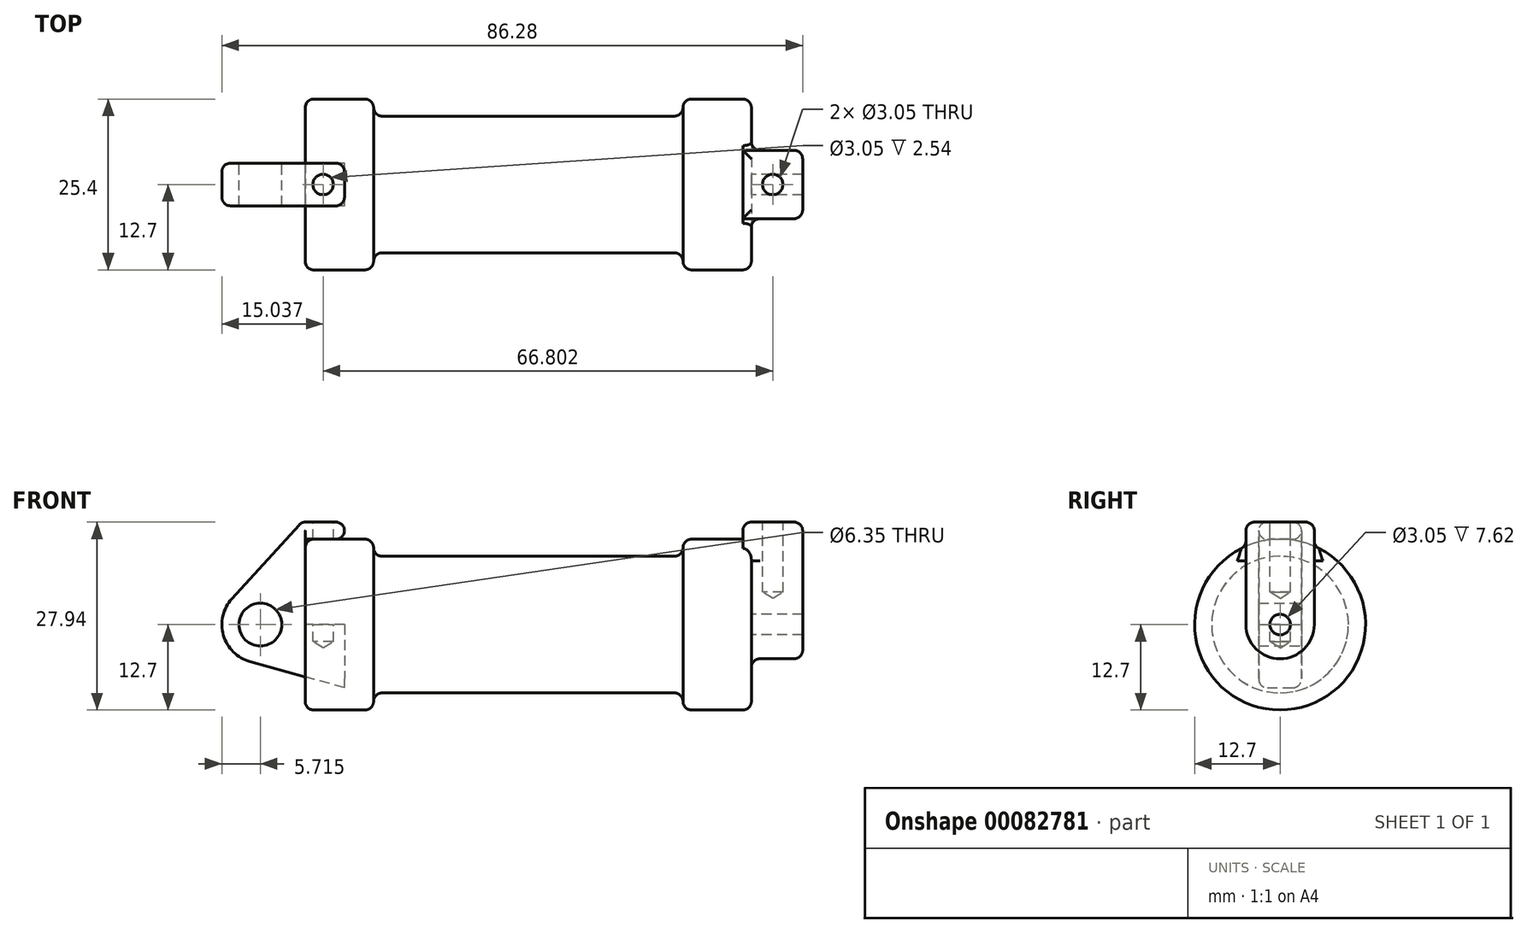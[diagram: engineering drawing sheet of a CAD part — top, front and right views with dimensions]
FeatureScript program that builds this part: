
annotation { "Feature Type Name" : "Feature", "Feature Type Description" : "" }
export const myFeature = defineFeature(function(context is Context, id is Id, definition is map)
    precondition{}
    {
        {
            var Q0;
            Q0=qCreatedBy(makeId("Front.planeOp"),FACE);
            var sketch = newSketch(context, id + "F0", { "sketchPlane" : qUnion([Q0])});
            skLineSegment(sketch, "E0", {"start": v(0, 0) * mm, "end": v(0, 12.7) * mm});
            skLineSegment(sketch, "E1", {"start": v(0, 12.7) * mm, "end": v(10.16, 12.7) * mm});
            skLineSegment(sketch, "E2", {"start": v(10.16, 12.7) * mm, "end": v(10.16, 10.16) * mm});
            skLineSegment(sketch, "E3", {"start": v(10.16, 10.16) * mm, "end": v(56.13, 10.16) * mm});
            skLineSegment(sketch, "E4", {"start": v(56.13, 10.16) * mm, "end": v(56.13, 12.7) * mm});
            skLineSegment(sketch, "E5", {"start": v(56.13, 12.7) * mm, "end": v(66.3, 12.7) * mm});
            skLineSegment(sketch, "E6", {"start": v(66.3, 12.7) * mm, "end": v(66.3, 0) * mm});
            skLineSegment(sketch, "E7", {"start": v(66.3, 0) * mm, "end": v(0, 0) * mm});
            skLineSegment(sketch, "E8", {"start": v(5.84, 15.24) * mm, "end": v(-0.5, 15.24) * mm});
            skLineSegment(sketch, "E9", {"start": v(-0.5, 15.24) * mm, "end": v(-10.88, 3.85) * mm});
            skLineSegment(sketch, "E10", {"start": v(0, 0) * mm, "end": v(-6.65, 0) * mm});
            skCircle(sketch, "E11", {"center": v(-6.65, 0) * mm, "radius": 5.72 * mm});
            skCircle(sketch, "E12", {"center": v(-6.65, 0) * mm, "radius": 3.18 * mm});
            skLineSegment(sketch, "E13", {"start": v(5.84, 15.24) * mm, "end": v(5.84, -9.4) * mm});
            skLineSegment(sketch, "E14", {"start": v(5.84, -9.4) * mm, "end": v(-8.18, -5.5) * mm});
            skSolve(sketch);
        }
        {
            var Q0;
            {var subQ0=sQuery(id+"F0.wireOp",EDGE,"E0");Q0=makeQuery(id+"F0.imprint","IMPRINT",FACE,{"disambiguationData":[TD([[makeQuery(id+"F0.imprint","IMPRINT",EDGE,{"derivedFrom":subQ0}),-1.0]])]});}
            var Q1;
            {var subQ0=sQuery(id+"F0.wireOp",EDGE,"E2");Q1=makeQuery(id+"F0.imprint","IMPRINT",FACE,{"disambiguationData":[TD([[makeQuery(id+"F0.imprint","IMPRINT",EDGE,{"derivedFrom":subQ0}),-1.0]])]});}
            var Q2;
            Q2=sQuery(id+"F0.wireOp",EDGE,"E7");
            revolve(context, id + "F1", {"entities" : qUnion([Q0, Q1]), "axis" : qUnion([Q2]), "revolveType" : RevolveType.FULL});
        }
        {
            var Q0;
            {var subQ3=sQuery(id+"F0.wireOp",EDGE,"E0");Q0=makeQuery(id+"F0.imprint","IMPRINT",FACE,{"disambiguationData":[TD([[makeQuery(id+"F0.imprint","IMPRINT",EDGE,{"derivedFrom":subQ3}),1.0]])]});}
            var Q1;
            {var subQ4=sQuery(id+"F0.wireOp",EDGE,"E12");Q1=makeQuery(id+"F0.imprint","IMPRINT",FACE,{"disambiguationData":[TD([[makeQuery(id+"F0.imprint","IMPRINT",EDGE,{"derivedFrom":subQ4}),-1.0]])]});}
            var Q2;
            {var subQ0=sQuery(id+"F0.wireOp",EDGE,"E14");Q2=makeQuery(id+"F0.imprint","IMPRINT",FACE,{"disambiguationData":[TD([[makeQuery(id+"F0.imprint","IMPRINT",EDGE,{"derivedFrom":subQ0}),-1.0]])]});}
            extrude(context, id + "F2", {"entities" : qUnion([Q0, Q1, Q2]), "endBound" : BoundingType.SYMMETRIC, "depth" : 6.35 * mm});
        }
        {
            var Q0;
            Q0=makeQuery(id+"F1.opRevolve","SWEPT_FACE",FACE,{"disambiguationData":[OSD([sQuery(id+"F0.wireOp",EDGE,"E6")])]});
            var sketch = newSketch(context, id + "F3", { "sketchPlane" : qUnion([Q0])});
            skCircle(sketch, "E15", {"center": v(0, 0) * mm, "radius": 5.08 * mm});
            skCircle(sketch, "E16", {"center": v(0, 0) * mm, "radius": 1.52 * mm});
            skLineSegment(sketch, "E17", {"start": v(-5.08, 0) * mm, "end": v(-5.08, 15.24) * mm});
            skLineSegment(sketch, "E18", {"start": v(5.08, 0) * mm, "end": v(5.08, 15.24) * mm});
            skLineSegment(sketch, "E19", {"start": v(5.08, 15.24) * mm, "end": v(-5.08, 15.24) * mm});
            skSolve(sketch);
        }
        {
            var Q0;
            {var subQ0=sQuery(id+"F3.wireOp",EDGE,"E19");Q0=makeQuery(id+"F3.imprint","IMPRINT",FACE,{"disambiguationData":[TD([[makeQuery(id+"F3.imprint","IMPRINT",EDGE,{"derivedFrom":subQ0}),1.0]])]});}
            var Q1;
            {var subQ0=sQuery(id+"F3.wireOp",EDGE,"E17");var subQ1=sQuery(id+"F3.wireOp",EDGE,"E15");var subQ2=makeQuery(id+"F3.imprint","INTERSECT",VERTEX,{"derivedFrom":[subQ1,subQ0]});Q1=makeQuery(id+"F3.imprint","IMPRINT",FACE,{"disambiguationData":[TD([[makeQuery(id+"F3.imprint","IMPRINT",EDGE,{"disambiguationData":[TD([[subQ2,1.0]])],"derivedFrom":subQ1}),-1.0]])]});}
            var Q2;
            Q2=makeQuery(id+"F3.imprint","IMPRINT",FACE,{"disambiguationData":[TD([[makeQuery(id+"F3.imprint","IMPRINT",EDGE,{"derivedFrom":sQuery(id+"F3.wireOp",EDGE,"E16")}),-1.0]])]});
            extrude(context, id + "F4", {"entities" : qUnion([Q0, Q1, Q2]), "operationType" : NewBodyOperationType.ADD, "depth" : 7.62 * mm, "hasSecondDirection" : true, "secondDirectionOppositeDirection" : true, "secondDirectionDepth" : 1.27 * mm});
        }
        {
            var Q0;
            Q0=makeQuery(id+"F4.opExtrude","SWEPT_FACE",FACE,{"disambiguationData":[OSD([sQuery(id+"F3.wireOp",EDGE,"E19")])]});
            var sketch = newSketch(context, id + "F5", { "sketchPlane" : qUnion([Q0])});
            skCircle(sketch, "E20", {"center": v(2.67, 0) * mm, "radius": 1.52 * mm});
            skPoint(sketch, "E20.centerSnap0", {"position": v(2.67, 3.18) * mm});
            skPoint(sketch, "E21.centerSnap0", {"position": v(69.47, 5.08) * mm});
            skSolve(sketch);
        }
        {
            var Q0;
            Q0=sQuery(id+"F5.wireOp",VERTEX,"E20.center");
            var Q1;
            Q1=makeQuery(id+"F2.opExtrude","SWEPT_BODY",BODY,{"disambiguationData":[OSD([sQuery(id+"F0.wireOp",EDGE,"E0"),sQuery(id+"F0.wireOp",EDGE,"E1"),sQuery(id+"F0.wireOp",EDGE,"E7"),sQuery(id+"F0.wireOp",EDGE,"E8"),sQuery(id+"F0.wireOp",EDGE,"E9"),sQuery(id+"F0.wireOp",EDGE,"E11"),sQuery(id+"F0.wireOp",EDGE,"E12"),sQuery(id+"F0.wireOp",EDGE,"E13"),sQuery(id+"F0.wireOp",EDGE,"E14")])]});
            hole(context, id + "F6", {"style" : HoleStyle.SIMPLE, "endStyle" : HoleEndStyle.BLIND, "holeDiameter" : 3.05 * mm, "holeDepth" : 17.78 * mm, "locations" : qUnion([Q0]), "scope" : qUnion([Q1])});
        }
        {
            var Q0;
            Q0=makeQuery(id+"F4.opExtrude","SWEPT_FACE",FACE,{"disambiguationData":[OSD([sQuery(id+"F3.wireOp",EDGE,"E19")])]});
            var sketch = newSketch(context, id + "F7", { "sketchPlane" : qUnion([Q0])});
            skCircle(sketch, "E22", {"center": v(69.47, 0) * mm, "radius": 1.52 * mm});
            skPoint(sketch, "E22.centerSnap0", {"position": v(69.47, 5.08) * mm});
            skPoint(sketch, "E22.centerSnap1", {"position": v(65.02, 0) * mm});
            skSolve(sketch);
        }
        {
            var Q0;
            Q0=sQuery(id+"F7.wireOp",VERTEX,"E22.center");
            var Q1;
            Q1=makeQuery(id+"F1.opRevolve","SWEPT_BODY",BODY,{"disambiguationData":[OSD([sQuery(id+"F0.wireOp",EDGE,"E0"),sQuery(id+"F0.wireOp",EDGE,"E1"),sQuery(id+"F0.wireOp",EDGE,"E2"),sQuery(id+"F0.wireOp",EDGE,"E3"),sQuery(id+"F0.wireOp",EDGE,"E4"),sQuery(id+"F0.wireOp",EDGE,"E5"),sQuery(id+"F0.wireOp",EDGE,"E6"),sQuery(id+"F0.wireOp",EDGE,"E7")])]});
            hole(context, id + "F8", {"style" : HoleStyle.SIMPLE, "endStyle" : HoleEndStyle.BLIND, "holeDiameter" : 3.05 * mm, "holeDepth" : 10.4 * mm, "locations" : qUnion([Q0]), "scope" : qUnion([Q1])});
        }
        {
            var Q0;
            Q0=makeQuery(id+"F1.opRevolve","SWEPT_EDGE",EDGE,{"disambiguationData":[OSD([sQuery(id+"F0.wireOp",EDGE,"E2"),sQuery(id+"F0.wireOp",EDGE,"E3")])]});
            var Q1;
            Q1=makeQuery(id+"F1.opRevolve","SWEPT_EDGE",EDGE,{"disambiguationData":[OSD([sQuery(id+"F0.wireOp",EDGE,"E1"),sQuery(id+"F0.wireOp",EDGE,"E2")])]});
            var Q2;
            Q2=makeQuery(id+"F1.opRevolve","SWEPT_EDGE",EDGE,{"disambiguationData":[OSD([sQuery(id+"F0.wireOp",EDGE,"E0"),sQuery(id+"F0.wireOp",EDGE,"E1")])]});
            var Q3;
            Q3=makeQuery(id+"F1.opRevolve","SWEPT_EDGE",EDGE,{"disambiguationData":[OSD([sQuery(id+"F0.wireOp",EDGE,"E4"),sQuery(id+"F0.wireOp",EDGE,"E5")])]});
            var Q4;
            Q4=makeQuery(id+"F1.opRevolve","SWEPT_EDGE",EDGE,{"disambiguationData":[OSD([sQuery(id+"F0.wireOp",EDGE,"E3"),sQuery(id+"F0.wireOp",EDGE,"E4")])]});
            var Q5;
            Q5=makeQuery(id+"F1.opRevolve","SWEPT_EDGE",EDGE,{"disambiguationData":[OSD([sQuery(id+"F0.wireOp",EDGE,"E5"),sQuery(id+"F0.wireOp",EDGE,"E6")])]});
            fillet(context, id + "F9", {"entities" : qUnion([Q0, Q1, Q2, Q3, Q4, Q5]), "radius" : 1.27 * mm, "tangentPropagation" : true, "allowEdgeOverflow" : false});
        }
        {
            var Q0;
            Q0=makeQuery(id+"F4.opExtrude","SWEPT_EDGE",EDGE,{"disambiguationData":[OSD([sQuery(id+"F3.wireOp",EDGE,"E17"),sQuery(id+"F3.wireOp",EDGE,"E19")])]});
            var Q1;
            Q1=makeQuery(id+"F4.opExtrude","CAP_EDGE",EDGE,{"disambiguationData":[OSD([sQuery(id+"F3.wireOp",EDGE,"E19")])],"isStart":true});
            var Q2;
            Q2=makeQuery(id+"F9.opFillet","BLEND_EDGE",EDGE,{"blendedFrom":[makeQuery(id+"F1.opRevolve","SWEPT_EDGE",EDGE,{"disambiguationData":[OSD([sQuery(id+"F0.wireOp",EDGE,"E5"),sQuery(id+"F0.wireOp",EDGE,"E6")])]}),makeQuery(id+"F4.opExtrude","SWEPT_FACE",FACE,{"disambiguationData":[OSD([sQuery(id+"F3.wireOp",EDGE,"E17")])]})],"blendedInto":[makeQuery(id+"F4.opExtrude","SWEPT_FACE",FACE,{"disambiguationData":[OSD([sQuery(id+"F3.wireOp",EDGE,"E17")])]})]});
            var Q3;
            Q3=makeQuery(id+"F4.boolean.opBoolean","INTERSECT",EDGE,{"derivedFrom":[makeQuery(id+"F1.opRevolve","SWEPT_FACE",FACE,{"disambiguationData":[OSD([sQuery(id+"F0.wireOp",EDGE,"E6")])]}),makeQuery(id+"F4.opExtrude","SWEPT_FACE",FACE,{"disambiguationData":[OSD([sQuery(id+"F3.wireOp",EDGE,"E17")])]})]});
            var Q4;
            Q4=makeQuery(id+"F4.opExtrude","SWEPT_EDGE",EDGE,{"disambiguationData":[OSD([sQuery(id+"F3.wireOp",EDGE,"E18"),sQuery(id+"F3.wireOp",EDGE,"E19")])]});
            var Q5;
            Q5=makeQuery(id+"F4.opExtrude","CAP_EDGE",EDGE,{"disambiguationData":[OSD([sQuery(id+"F3.wireOp",EDGE,"E19")])],"isStart":false});
            var Q6;
            Q6=makeQuery(id+"F4.opExtrude","CAP_EDGE",EDGE,{"disambiguationData":[OSD([sQuery(id+"F3.wireOp",EDGE,"E17")])],"isStart":false});
            var Q7;
            Q7=makeQuery(id+"F4.opExtrude","CAP_EDGE",EDGE,{"disambiguationData":[OSD([sQuery(id+"F3.wireOp",EDGE,"E18")])],"isStart":false});
            fillet(context, id + "F10", {"entities" : qUnion([Q0, Q1, Q2, Q3, Q4, Q5, Q6, Q7]), "radius" : 1.27 * mm, "tangentPropagation" : true, "allowEdgeOverflow" : false});
        }
        {
            var Q0;
            Q0=makeQuery(id+"F2.opExtrude","CAP_EDGE",EDGE,{"disambiguationData":[OSD([sQuery(id+"F0.wireOp",EDGE,"E8")])],"isStart":false});
            var Q1;
            Q1=makeQuery(id+"F2.opExtrude","SWEPT_EDGE",EDGE,{"disambiguationData":[OSD([sQuery(id+"F0.wireOp",EDGE,"E8"),sQuery(id+"F0.wireOp",EDGE,"E9")])]});
            var Q2;
            Q2=makeQuery(id+"F2.opExtrude","SWEPT_EDGE",EDGE,{"disambiguationData":[OSD([sQuery(id+"F0.wireOp",EDGE,"E8"),sQuery(id+"F0.wireOp",EDGE,"E13")])]});
            var Q3;
            {var subQ0=sQuery(id+"F0.wireOp",EDGE,"E13");Q3=makeQuery(id+"F2.opExtrude","CAP_EDGE",EDGE,{"disambiguationData":[OSD([subQ0]),TDD([makeQuery(id+"F0.imprint","IMPRINT",EDGE,{"disambiguationData":[TD([[makeQuery(id+"F0.imprint","INTERSECT",VERTEX,{"derivedFrom":[sQuery(id+"F0.wireOp",EDGE,"E8"),subQ0]}),-1.0]])],"derivedFrom":subQ0})])],"isStart":false});}
            var Q4;
            Q4=makeQuery(id+"F2.opExtrude","CAP_EDGE",EDGE,{"disambiguationData":[OSD([sQuery(id+"F0.wireOp",EDGE,"E9")])],"isStart":false});
            var Q5;
            Q5=makeQuery(id+"F2.opExtrude","CAP_EDGE",EDGE,{"disambiguationData":[OSD([sQuery(id+"F0.wireOp",EDGE,"E9")])],"isStart":true});
            var Q6;
            {var subQ0=sQuery(id+"F0.wireOp",EDGE,"E13");Q6=makeQuery(id+"F2.opExtrude","CAP_EDGE",EDGE,{"disambiguationData":[OSD([subQ0]),TDD([makeQuery(id+"F0.imprint","IMPRINT",EDGE,{"disambiguationData":[TD([[makeQuery(id+"F0.imprint","INTERSECT",VERTEX,{"derivedFrom":[sQuery(id+"F0.wireOp",EDGE,"E8"),subQ0]}),-1.0]])],"derivedFrom":subQ0})])],"isStart":true});}
            var Q7;
            Q7=makeQuery(id+"F1.opRevolve","SWEPT_FACE",FACE,{"disambiguationData":[OSD([sQuery(id+"F0.wireOp",EDGE,"E1")])]});
            var Q8;
            Q8=makeQuery(id+"F2.opExtrude","CAP_EDGE",EDGE,{"disambiguationData":[OSD([sQuery(id+"F0.wireOp",EDGE,"E8")])],"isStart":true});
            fillet(context, id + "F11", {"entities" : qUnion([Q0, Q1, Q2, Q3, Q4, Q5, Q6, Q7, Q8]), "radius" : 1.27 * mm, "tangentPropagation" : true, "allowEdgeOverflow" : false});
        }
        {
            var Q0;
            Q0=makeQuery(id+"F2.opExtrude","CAP_EDGE",EDGE,{"disambiguationData":[OSD([sQuery(id+"F0.wireOp",EDGE,"E1")])],"isStart":true});
            fillet(context, id + "F12", {"entities" : qUnion([Q0]), "radius" : 1.27 * mm, "tangentPropagation" : true, "allowEdgeOverflow" : false});
        }
    });
